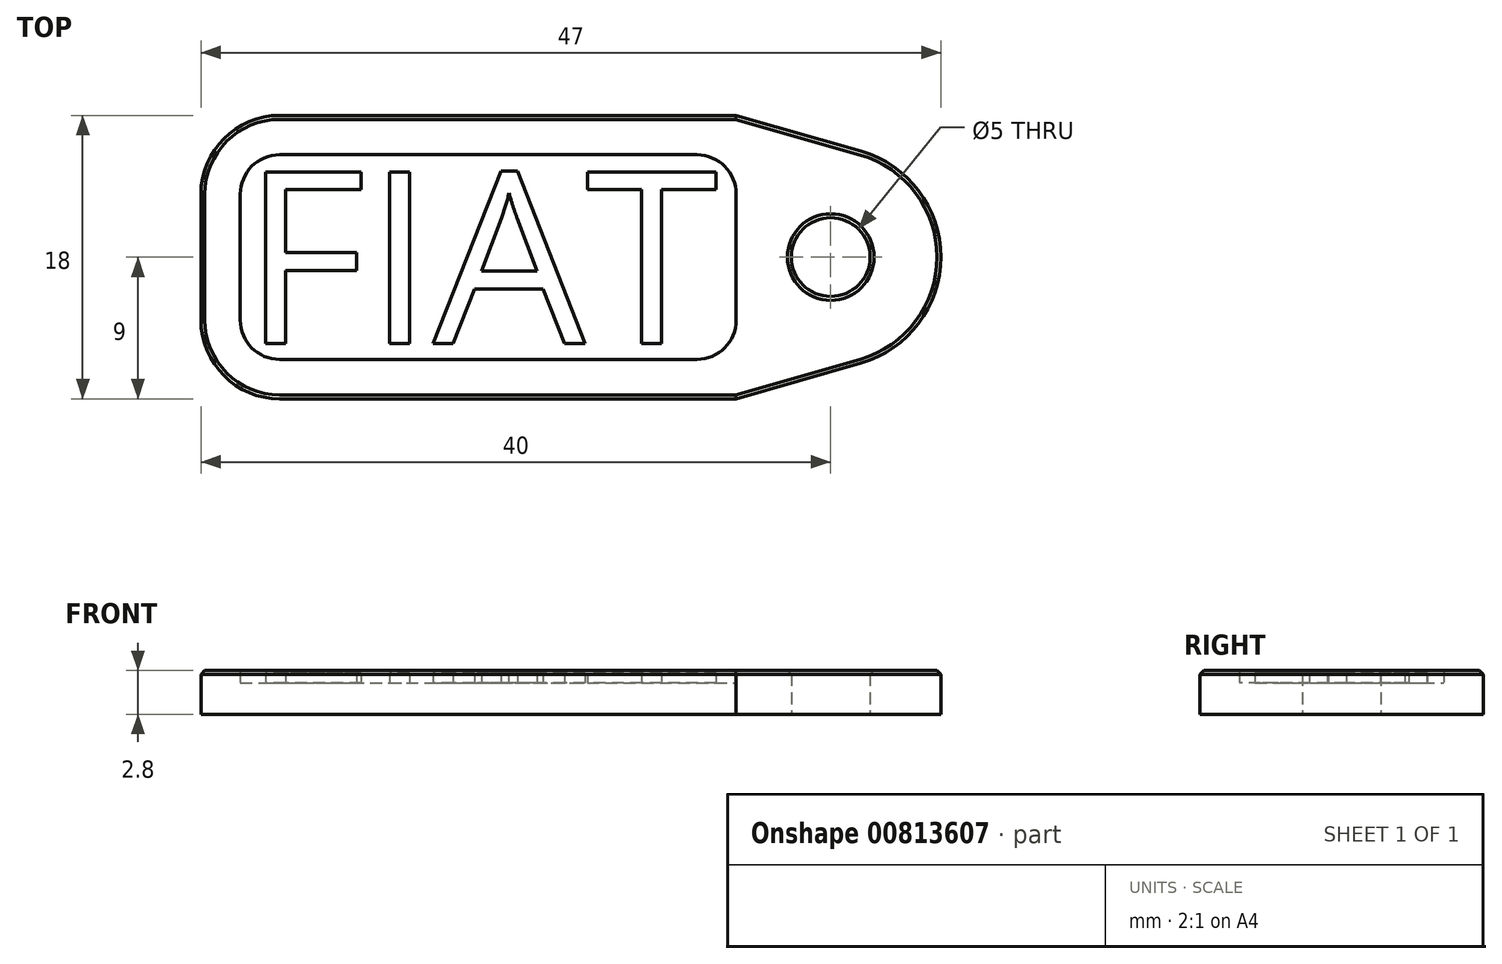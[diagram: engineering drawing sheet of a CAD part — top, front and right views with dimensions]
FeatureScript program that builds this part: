
annotation { "Feature Type Name" : "Feature", "Feature Type Description" : "" }
export const myFeature = defineFeature(function(context is Context, id is Id, definition is map)
    precondition{}
    {
        {
            var Q0;
            Q0=qCreatedBy(makeId("Top.planeOp"),FACE);
            var sketch = newSketch(context, id + "F0", { "sketchPlane" : qUnion([Q0])});
            skLineSegment(sketch, "E0", {"start": v(5, 9) * mm, "end": v(34, 9) * mm});
            skLineSegment(sketch, "E1", {"start": v(34, 9) * mm, "end": v(41.93, 6.73) * mm});
            skLineSegment(sketch, "E2", {"start": v(41.93, -6.73) * mm, "end": v(34, -9) * mm});
            skLineSegment(sketch, "E3", {"start": v(34, -9) * mm, "end": v(5, -9) * mm});
            skLineSegment(sketch, "E4", {"start": v(0, -4) * mm, "end": v(0, 4) * mm});
            skPoint(sketch, "E5.visualSharp", {"position": v(65.42, 0) * mm});
            skArc(sketch, "E5.filletArc", {"start": v(41.93, -6.73) * mm, "mid": v(47, 0) * mm, "end": v(41.93, 6.73) * mm});
            skPoint(sketch, "E6.visualSharp", {"position": v(0, 9) * mm});
            skArc(sketch, "E6.filletArc", {"start": v(5, 9) * mm, "mid": v(1.46, 7.54) * mm, "end": v(0, 4) * mm});
            skPoint(sketch, "E7.visualSharp", {"position": v(0, -9) * mm});
            skArc(sketch, "E7.filletArc", {"start": v(0, -4) * mm, "mid": v(1.46, -7.54) * mm, "end": v(5, -9) * mm});
            skSolve(sketch);
        }
        {
            var Q0;
            Q0=makeQuery(id+"F0.imprint","IMPRINT",FACE,{"disambiguationData":[TD([[makeQuery(id+"F0.imprint","IMPRINT",EDGE,{"derivedFrom":sQuery(id+"F0.wireOp",EDGE,"E0")}),-1.0]])]});
            extrude(context, id + "F1", {"entities" : qUnion([Q0]), "depth" : 2 * mm, "offsetDistance" : 25 * mm});
        }
        {
            var Q0;
            Q0=sQuery(id+"F0.wireOp",VERTEX,"E5.filletArc.center");
            var Q1;
            Q1=makeQuery(id+"F1.opExtrude","SWEPT_BODY",BODY,{"disambiguationData":[OSD([sQuery(id+"F0.wireOp",EDGE,"E0"),sQuery(id+"F0.wireOp",EDGE,"E1"),sQuery(id+"F0.wireOp",EDGE,"E2"),sQuery(id+"F0.wireOp",EDGE,"E3"),sQuery(id+"F0.wireOp",EDGE,"E4"),sQuery(id+"F0.wireOp",EDGE,"E5.filletArc"),sQuery(id+"F0.wireOp",EDGE,"E6.filletArc"),sQuery(id+"F0.wireOp",EDGE,"E7.filletArc")])]});
            hole(context, id + "F2", {"style" : HoleStyle.SIMPLE, "endStyle" : HoleEndStyle.THROUGH, "oppositeDirection" : true, "holeDiameter" : 5 * mm, "majorDiameter" : 5 * mm, "isTappedThrough" : true, "tappedDepth" : 12 * mm, "tapClearance" : 3, "locations" : qUnion([Q0]), "scope" : qUnion([Q1])});
        }
        {
            var Q0;
            Q0=makeQuery(id+"F1.opExtrude","CAP_FACE",FACE,{"disambiguationData":[OSD([sQuery(id+"F0.wireOp",EDGE,"E0"),sQuery(id+"F0.wireOp",EDGE,"E1"),sQuery(id+"F0.wireOp",EDGE,"E2"),sQuery(id+"F0.wireOp",EDGE,"E3"),sQuery(id+"F0.wireOp",EDGE,"E4"),sQuery(id+"F0.wireOp",EDGE,"E5.filletArc"),sQuery(id+"F0.wireOp",EDGE,"E6.filletArc"),sQuery(id+"F0.wireOp",EDGE,"E7.filletArc")])],"isStart":false});
            var sketch = newSketch(context, id + "F3", { "sketchPlane" : qUnion([Q0])});
            skLineSegment(sketch, "E8", {"start": v(2.5, 4) * mm, "end": v(2.5, -4) * mm});
            skLineSegment(sketch, "E9", {"start": v(5, -6.5) * mm, "end": v(31.5, -6.5) * mm});
            skLineSegment(sketch, "E10", {"start": v(34, -4) * mm, "end": v(34, 4) * mm});
            skLineSegment(sketch, "E11", {"start": v(31.5, 6.5) * mm, "end": v(5, 6.5) * mm});
            skPoint(sketch, "E12.visualSharp", {"position": v(2.5, 6.5) * mm});
            skArc(sketch, "E12.filletArc", {"start": v(5, 6.5) * mm, "mid": v(3.23, 5.77) * mm, "end": v(2.5, 4) * mm});
            skPoint(sketch, "E13.visualSharp", {"position": v(2.5, -6.5) * mm});
            skArc(sketch, "E13.filletArc", {"start": v(2.5, -4) * mm, "mid": v(3.23, -5.77) * mm, "end": v(5, -6.5) * mm});
            skPoint(sketch, "E14.visualSharp", {"position": v(34, -6.5) * mm});
            skArc(sketch, "E14.filletArc", {"start": v(31.5, -6.5) * mm, "mid": v(33.27, -5.77) * mm, "end": v(34, -4) * mm});
            skPoint(sketch, "E15.visualSharp", {"position": v(34, 6.5) * mm});
            skArc(sketch, "E15.filletArc", {"start": v(34, 4) * mm, "mid": v(33.27, 5.77) * mm, "end": v(31.5, 6.5) * mm});
            skText(sketch, "E16", { "text": "FIAT", "fontName": "OpenSans-Regular.ttf"});
            const initialGuessF3  = {"E16": [0.0026, -0.0055, 1, 0, 0.011]};
            skSetInitialGuess(sketch, initialGuessF3);
            skSolve(sketch);
        }
        {
            var Q0;
            Q0=makeQuery(id+"F3.imprint","IMPRINT",FACE,{"disambiguationData":[TD([[makeQuery(id+"F3.imprint","IMPRINT",EDGE,{"derivedFrom":sQuery(id+"F3.wireOp",EDGE,"E16.sketch_text.stroke-0")}),-1.0]])]});
            var Q1;
            Q1=makeQuery(id+"F3.imprint","IMPRINT",FACE,{"disambiguationData":[TD([[makeQuery(id+"F3.imprint","IMPRINT",EDGE,{"derivedFrom":sQuery(id+"F3.wireOp",EDGE,"E16.sketch_text.stroke-10")}),-1.0]])]});
            var Q2;
            Q2=makeQuery(id+"F3.imprint","IMPRINT",FACE,{"disambiguationData":[TD([[makeQuery(id+"F3.imprint","IMPRINT",EDGE,{"derivedFrom":sQuery(id+"F3.wireOp",EDGE,"E16.sketch_text.stroke-27")}),-1.0]])]});
            var Q3;
            Q3=makeQuery(id+"F3.imprint","IMPRINT",FACE,{"disambiguationData":[TD([[makeQuery(id+"F3.imprint","IMPRINT",EDGE,{"derivedFrom":sQuery(id+"F3.wireOp",EDGE,"E16.sketch_text.stroke-14")}),-1.0]])]});
            extrude(context, id + "F4", {"entities" : qUnion([Q0, Q1, Q2, Q3]), "operationType" : NewBodyOperationType.ADD, "depth" : .6 * mm, "offsetDistance" : 25 * mm});
        }
        {
            var Q0;
            Q0=makeQuery(id+"F3.imprint","IMPRINT",FACE,{"disambiguationData":[TD([[makeQuery(id+"F3.imprint","IMPRINT",EDGE,{"derivedFrom":sQuery(id+"F3.wireOp",EDGE,"E8")}),-1.0]])]});
            extrude(context, id + "F5", {"entities" : qUnion([Q0]), "operationType" : NewBodyOperationType.ADD, "depth" : .8 * mm, "offsetDistance" : 25 * mm});
        }
        {
            var Q0;
            Q0=makeQuery(id+"F5.opExtrude","CAP_EDGE",EDGE,{"disambiguationData":[OSD([sQuery(id+"F0.wireOp",EDGE,"E3")])],"isStart":false});
            var Q1;
            Q1=makeQuery(id+"F5.opExtrude","CAP_EDGE",EDGE,{"disambiguationData":[OSD([sQuery(id+"F0.wireOp",EDGE,"E2")])],"isStart":false});
            var Q2;
            Q2=makeQuery(id+"F5.opExtrude","CAP_EDGE",EDGE,{"disambiguationData":[OSD([sQuery(id+"F0.wireOp",EDGE,"E0"),sQuery(id+"F0.wireOp",EDGE,"E1"),sQuery(id+"F0.wireOp",EDGE,"E2"),sQuery(id+"F0.wireOp",EDGE,"E3"),sQuery(id+"F0.wireOp",EDGE,"E4"),sQuery(id+"F0.wireOp",EDGE,"E5.filletArc"),sQuery(id+"F0.wireOp",EDGE,"E6.filletArc"),sQuery(id+"F0.wireOp",EDGE,"E7.filletArc"),sQuery(id+"F2.hole-0.sketch.wireOp",EDGE,"core_line_2")])],"isStart":false});
            chamfer(context, id + "F6", {"entities" : qUnion([Q0, Q1, Q2]), "width" : .25 * mm, "tangentPropagation" : true});
        }
    });
